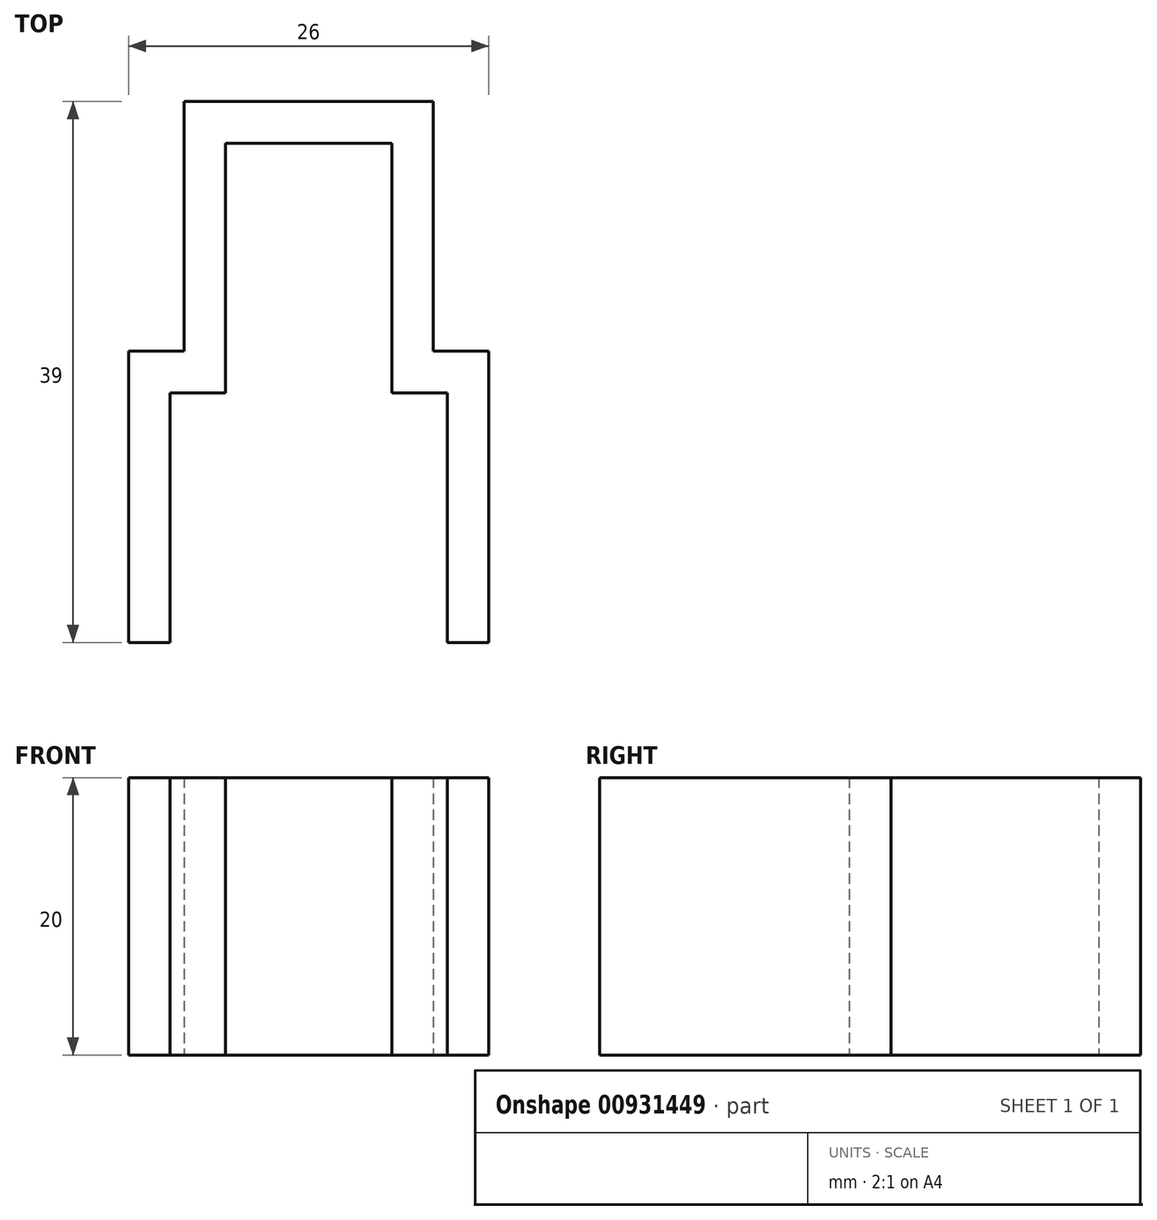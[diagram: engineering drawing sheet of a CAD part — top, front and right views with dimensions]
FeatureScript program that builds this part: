
annotation { "Feature Type Name" : "Feature", "Feature Type Description" : "" }
export const myFeature = defineFeature(function(context is Context, id is Id, definition is map)
    precondition{}
    {
        {
            var Q0;
            Q0=qCreatedBy(makeId("Top.planeOp"),FACE);
            var sketch = newSketch(context, id + "F0", { "sketchPlane" : qUnion([Q0])});
            skLineSegment(sketch, "E0.top", {"start": v(-6, 9) * mm, "end": v(6, 9) * mm});
            skLineSegment(sketch, "E0.left", {"start": v(-6, -9) * mm, "end": v(-6, 9) * mm});
            skLineSegment(sketch, "E0.right", {"start": v(6, -9) * mm, "end": v(6, 9) * mm});
            skPoint(sketch, "E0.middle", {"position": v(0, 0) * mm});
            skLineSegment(sketch, "E1.top", {"start": v(-10, -9) * mm, "end": v(-6, -9) * mm});
            skLineSegment(sketch, "E1.left", {"start": v(-10, -27) * mm, "end": v(-10, -9) * mm});
            skLineSegment(sketch, "E1.right", {"start": v(10, -27) * mm, "end": v(10, -9) * mm});
            skPoint(sketch, "E1.middle", {"position": v(0, -18) * mm});
            skPoint(sketch, "E1.middle.positionSnap0", {"position": v(0, -9) * mm});
            skPoint(sketch, "E1.centerSnap0", {"position": v(0, -9) * mm});
            skLineSegment(sketch, "E2.trimOffspring", {"start": v(6, -9) * mm, "end": v(10, -9) * mm});
            skLineSegment(sketch, "E3.0", {"start": v(13, -27) * mm, "end": v(13, -6) * mm});
            skLineSegment(sketch, "E3.1", {"start": v(9, -6) * mm, "end": v(13, -6) * mm});
            skLineSegment(sketch, "E3.2", {"start": v(9, -6) * mm, "end": v(9, 12) * mm});
            skLineSegment(sketch, "E3.3", {"start": v(-13, -27) * mm, "end": v(-13, -6) * mm});
            skLineSegment(sketch, "E3.4", {"start": v(-13, -6) * mm, "end": v(-9, -6) * mm});
            skLineSegment(sketch, "E3.5", {"start": v(-9, -6) * mm, "end": v(-9, 12) * mm});
            skLineSegment(sketch, "E3.6", {"start": v(-9, 12) * mm, "end": v(9, 12) * mm});
            skLineSegment(sketch, "E4", {"start": v(-13, -27) * mm, "end": v(-10, -27) * mm});
            skLineSegment(sketch, "E5", {"start": v(10, -27) * mm, "end": v(13, -27) * mm});
            skSolve(sketch);
        }
        {
            var Q0;
            Q0 = qSketchRegion(id + "F0", true);
            extrude(context, id + "F1", {"entities" : qUnion([Q0]), "depth" : 20 * mm, "offsetDistance" : 25 * mm});
        }
    });
